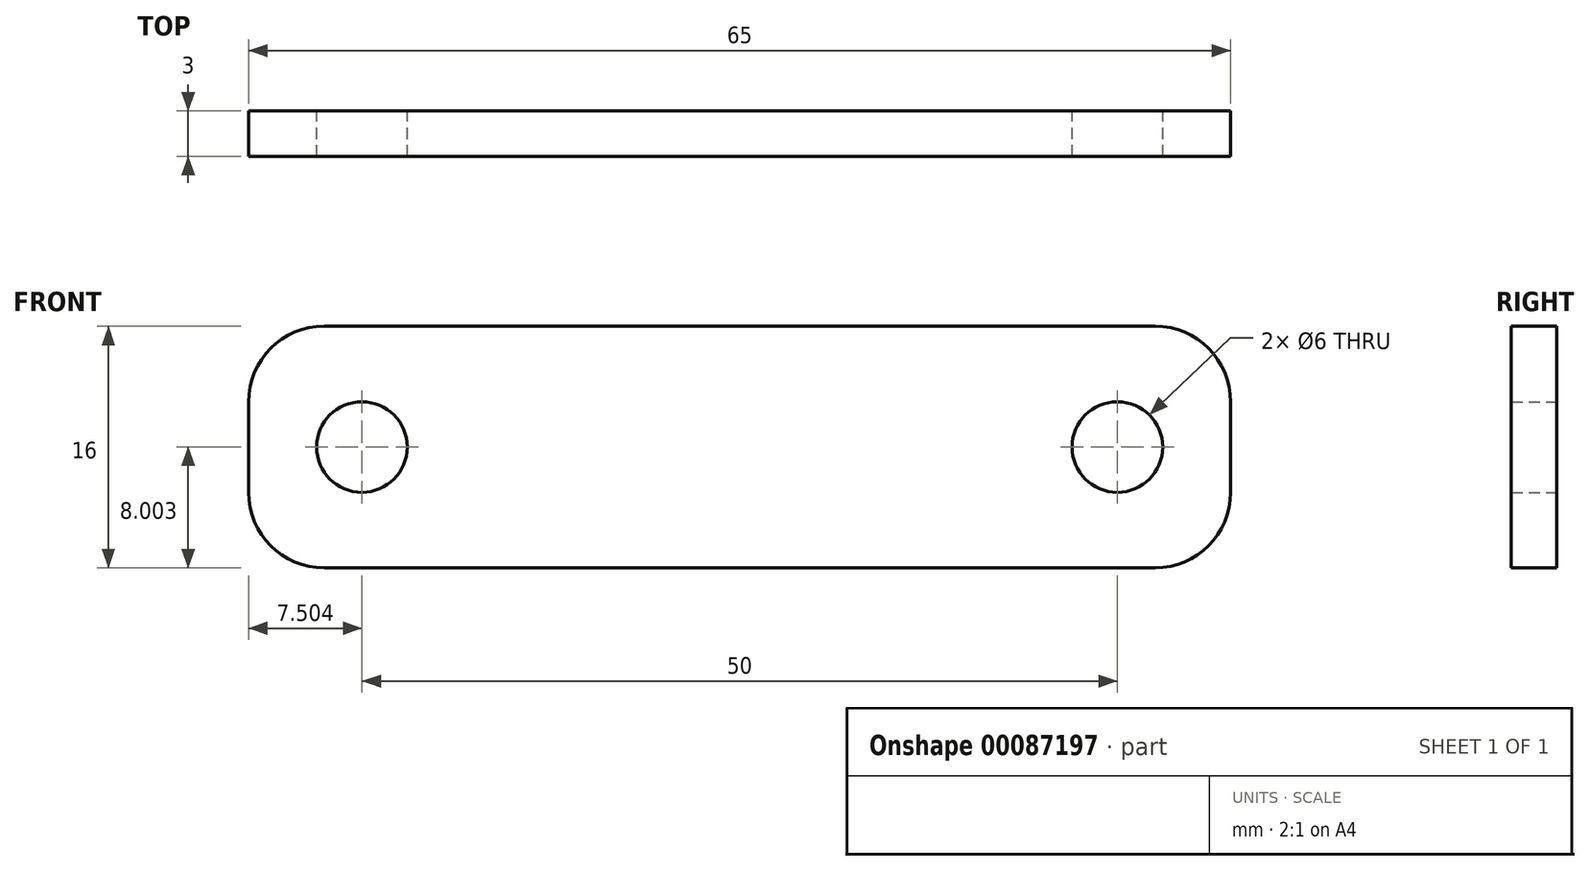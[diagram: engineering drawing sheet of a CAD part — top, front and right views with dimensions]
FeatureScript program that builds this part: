
annotation { "Feature Type Name" : "Feature", "Feature Type Description" : "" }
export const myFeature = defineFeature(function(context is Context, id is Id, definition is map)
    precondition{}
    {
        {
            var Q0;
            Q0=qCreatedBy(makeId("Front.planeOp"),FACE);
            var sketch = newSketch(context, id + "F0", { "sketchPlane" : qUnion([Q0])});
            skLineSegment(sketch, "E0", {"start": v(-172.94, 33.38) * mm, "end": v(-122.94, 33.38) * mm, "construction": true});
            skCircle(sketch, "E1", {"center": v(-172.94, 33.38) * mm, "radius": 3 * mm});
            skCircle(sketch, "E2", {"center": v(-122.94, 33.38) * mm, "radius": 3 * mm});
            skLineSegment(sketch, "E3.bottom", {"start": v(-120.44, 41.38) * mm, "end": v(-175.44, 41.38) * mm});
            skLineSegment(sketch, "E3.top", {"start": v(-120.44, 25.38) * mm, "end": v(-175.44, 25.38) * mm});
            skLineSegment(sketch, "E3.left", {"start": v(-115.44, 36.38) * mm, "end": v(-115.44, 30.38) * mm});
            skLineSegment(sketch, "E3.right", {"start": v(-180.44, 36.38) * mm, "end": v(-180.44, 30.38) * mm});
            skPoint(sketch, "E3.middle", {"position": v(-147.94, 33.38) * mm});
            skPoint(sketch, "E4.visualSharp", {"position": v(-115.44, 41.38) * mm});
            skArc(sketch, "E4.filletArc", {"start": v(-115.44, 36.38) * mm, "mid": v(-116.9, 39.92) * mm, "end": v(-120.44, 41.38) * mm});
            skPoint(sketch, "E5.visualSharp", {"position": v(-115.44, 25.38) * mm});
            skArc(sketch, "E5.filletArc", {"start": v(-120.44, 25.38) * mm, "mid": v(-116.9, 26.85) * mm, "end": v(-115.44, 30.38) * mm});
            skPoint(sketch, "E6.visualSharp", {"position": v(-180.44, 25.38) * mm});
            skArc(sketch, "E6.filletArc", {"start": v(-180.44, 30.38) * mm, "mid": v(-178.97, 26.85) * mm, "end": v(-175.44, 25.38) * mm});
            skPoint(sketch, "E7.visualSharp", {"position": v(-180.44, 41.38) * mm});
            skArc(sketch, "E7.filletArc", {"start": v(-175.44, 41.38) * mm, "mid": v(-178.97, 39.92) * mm, "end": v(-180.44, 36.38) * mm});
            skSolve(sketch);
        }
        {
            var Q0;
            Q0=qSketchRegion(id+"F0",true);
            extrude(context, id + "F1", {"entities" : qUnion([Q0]), "depth" : 3 * mm});
        }
    });
